# Revit family: Maxlogic Conventional Sounder expansion panel
name_source: partatom
category: Fire Alarm Devices
units: mm (PartAtom-declared; Revit-internal decimal feet)

## family parameters
Cut with Voids When Loaded = No
Host = Face
Maintain Annotation Orientation = Yes
OmniClass Number = 23.85.30.21
OmniClass Title = Environmental Detection/Registration
Part Type = Normal
Room Calculation Point = No
Round Connector Dimension = Use Diameter
Shared = No

## types (1)
- Maxlogic Conventional Sounder expansion panel
    Battery = 2 X (12V DC 7 Ah )
    Code Performance = EN 54-4 / EN 54-18
    Color = White
    Cost = 0 $
    Default Elevation = 0 mm  [stored 0 ft]
    Description = Conventional Sounder expansion panel
    External supply = 220 V AC
    Fax Number = (+)90 216 466 45 10
    Installation Manual = https://mavilielektronik.com
    Main Material = Metal Grey
    Manufacturer = Mavili Elektronik Ticaret A.Ş.
    Model = Maxlogic
    Mounting surface = Wall mount
    Nominal Depth = 130 mm
    Nominal Height = 300 mm
    Nominal Width = 400 mm
    Operating temperature = (-5°C) - (+50°C)
    Product Code = ML-0314
    Secondary Material = White Plastic ABS
    URL = https://www.mavili.com.tr
    Warranty Duration Labor = 2
    Warranty Duration Parts = 2
    Warranty Duration Unit = Year

note: [stored X ft] marks values corroborated as IEEE doubles in the binary element streams (Revit-internal decimal feet)

## geometry (parser evidence)
native form markers: Sweep x2
no freeform markers — native parametric forms only
